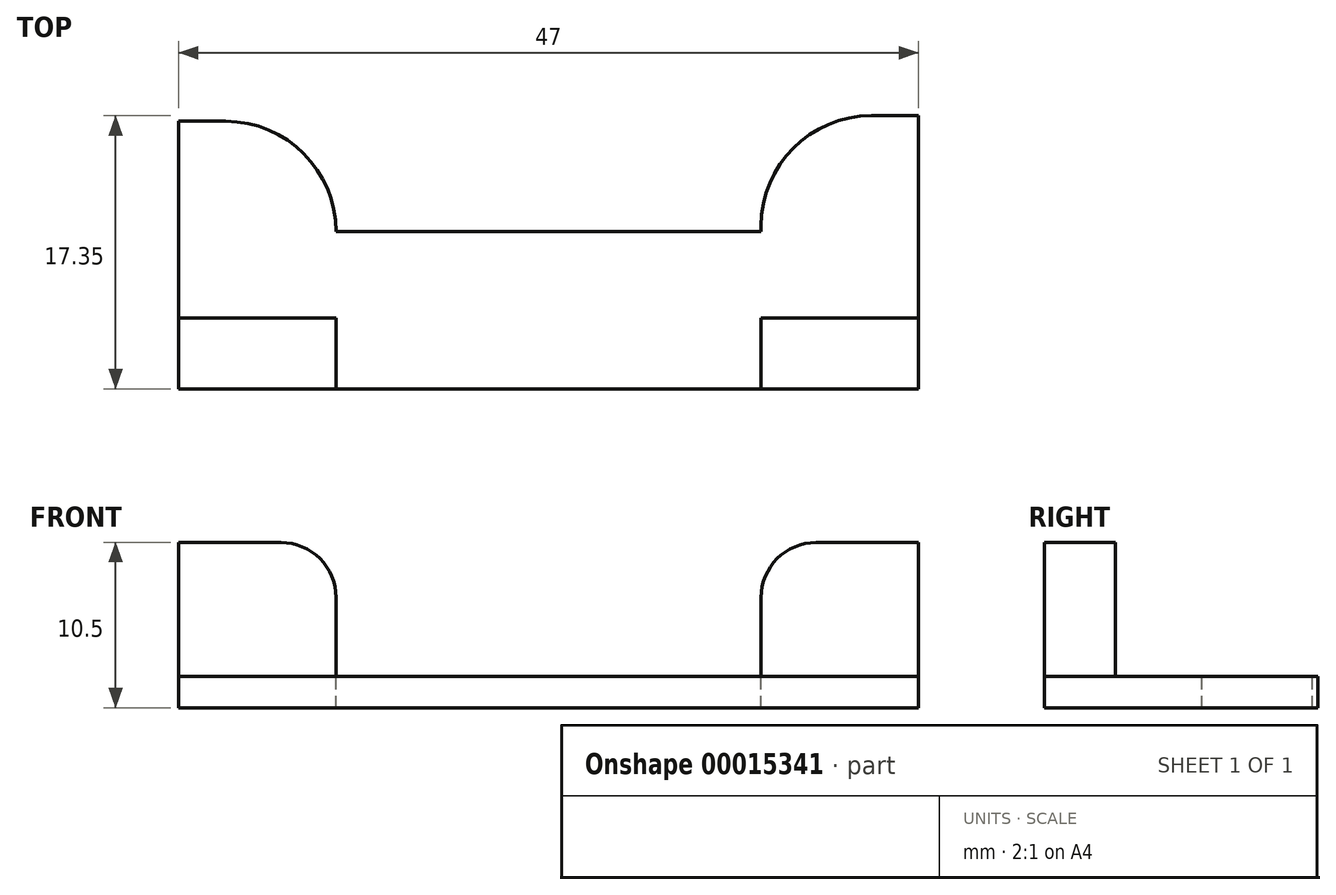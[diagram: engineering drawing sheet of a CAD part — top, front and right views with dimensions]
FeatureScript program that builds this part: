
annotation { "Feature Type Name" : "Feature", "Feature Type Description" : "" }
export const myFeature = defineFeature(function(context is Context, id is Id, definition is map)
    precondition{}
    {
        {
            var Q0;
            Q0=qCreatedBy(makeId("Top.planeOp"),FACE);
            var sketch = newSketch(context, id + "F0", { "sketchPlane" : qUnion([Q0])});
            skLineSegment(sketch, "E0", {"start": v(0, 0) * mm, "end": v(-47, 0) * mm});
            skLineSegment(sketch, "E1", {"start": v(-47, 0) * mm, "end": v(-47, 17) * mm});
            skLineSegment(sketch, "E2", {"start": v(-37, 10) * mm, "end": v(-10, 10) * mm});
            skLineSegment(sketch, "E3", {"start": v(0, 17.35) * mm, "end": v(0, 0) * mm});
            skLineSegment(sketch, "E4", {"start": v(-37, 10) * mm, "end": v(-37, 7) * mm, "construction": true});
            skLineSegment(sketch, "E5", {"start": v(-37, 7) * mm, "end": v(0, 7) * mm, "construction": true});
            skPoint(sketch, "E6.visualSharp", {"position": v(-37, 17) * mm});
            skPoint(sketch, "E7.visualSharp", {"position": v(-10, 17.35) * mm});
            skLineSegment(sketch, "E8", {"start": v(-10, 9.85) * mm, "end": v(-10, 10) * mm});
            skLineSegment(sketch, "E9", {"start": v(-47, 17) * mm, "end": v(-44, 17) * mm});
            skLineSegment(sketch, "E10", {"start": v(-37, 10) * mm, "end": v(-37, 10) * mm});
            skArc(sketch, "E11.filletArc", {"start": v(-37, 10) * mm, "mid": v(-39.05, 14.95) * mm, "end": v(-44, 17) * mm});
            skLineSegment(sketch, "E12", {"start": v(-10, 10) * mm, "end": v(-10, 10.35) * mm});
            skLineSegment(sketch, "E13", {"start": v(0, 17.35) * mm, "end": v(-3, 17.35) * mm});
            skArc(sketch, "E14.filletArc", {"start": v(-3, 17.35) * mm, "mid": v(-7.95, 15.3) * mm, "end": v(-10, 10.35) * mm});
            skSolve(sketch);
        }
        {
            var Q0;
            Q0=qSketchRegion(id+"F0",true);
            extrude(context, id + "F1", {"entities" : qUnion([Q0]), "oppositeDirection" : true, "depth" : 2 * mm});
        }
        {
            var Q0;
            Q0=makeQuery(id+"F1.opExtrude","SWEPT_FACE",FACE,{"disambiguationData":[OSD([sQuery(id+"F0.wireOp",EDGE,"E0")])]});
            var sketch = newSketch(context, id + "F2", { "sketchPlane" : qUnion([Q0])});
            skLineSegment(sketch, "E15", {"start": v(0, 0) * mm, "end": v(0, 8.5) * mm});
            skLineSegment(sketch, "E16", {"start": v(0, 8.5) * mm, "end": v(-47, 8.5) * mm, "construction": true});
            skLineSegment(sketch, "E17", {"start": v(-47, 8.5) * mm, "end": v(-47, 0) * mm});
            skLineSegment(sketch, "E18", {"start": v(0, 8.5) * mm, "end": v(-6.5, 8.5) * mm});
            skLineSegment(sketch, "E19", {"start": v(-47, 8.5) * mm, "end": v(-40.5, 8.5) * mm});
            skPoint(sketch, "E20.visualSharp", {"position": v(-10, 8.5) * mm});
            skArc(sketch, "E20.filletArc", {"start": v(-6.5, 8.5) * mm, "mid": v(-8.97, 7.47) * mm, "end": v(-10, 5) * mm});
            skPoint(sketch, "E21.visualSharp", {"position": v(-37, 8.5) * mm});
            skArc(sketch, "E21.filletArc", {"start": v(-37, 5) * mm, "mid": v(-38.03, 7.47) * mm, "end": v(-40.5, 8.5) * mm});
            skLineSegment(sketch, "E22", {"start": v(0, 0) * mm, "end": v(-47, 0) * mm});
            skLineSegment(sketch, "E23", {"start": v(-10, 5) * mm, "end": v(-10, 0) * mm});
            skLineSegment(sketch, "E24", {"start": v(-37, 5) * mm, "end": v(-37, 0) * mm});
            skLineSegment(sketch, "E25", {"start": v(-37, 0) * mm, "end": v(-10, 0) * mm});
            skSolve(sketch);
        }
        {
            var Q0;
            Q0=qSketchRegion(id+"F2",true);
            extrude(context, id + "F3", {"entities" : qUnion([Q0]), "oppositeDirection" : true, "depth" : 4.5 * mm});
        }
    });
